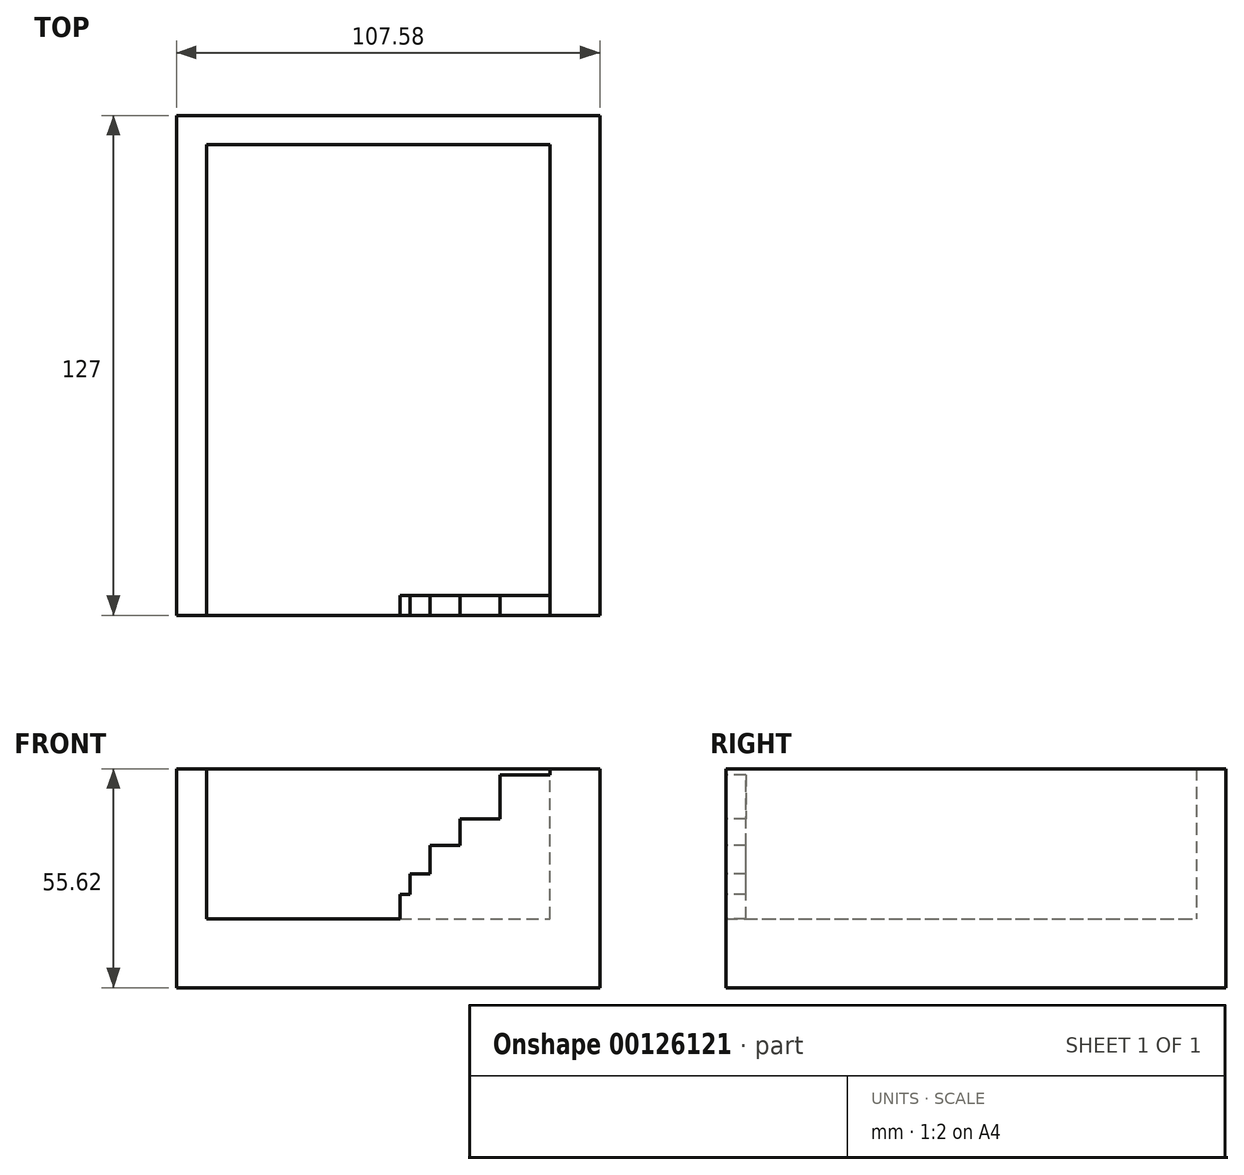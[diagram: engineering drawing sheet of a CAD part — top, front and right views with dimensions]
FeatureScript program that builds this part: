
annotation { "Feature Type Name" : "Feature", "Feature Type Description" : "" }
export const myFeature = defineFeature(function(context is Context, id is Id, definition is map)
    precondition{}
    {
        {
            var Q0;
            Q0=qCreatedBy(makeId("Front.planeOp"),FACE);
            var sketch = newSketch(context, id + "F0", { "sketchPlane" : qUnion([Q0])});
            skLineSegment(sketch, "E0.bottom", {"start": v(-64.64, -20.85) * mm, "end": v(42.94, -20.85) * mm});
            skLineSegment(sketch, "E0.top", {"start": v(-64.64, -3.33) * mm, "end": v(42.94, -3.33) * mm});
            skLineSegment(sketch, "E0.left", {"start": v(-64.64, -20.85) * mm, "end": v(-64.64, -3.33) * mm});
            skLineSegment(sketch, "E0.right", {"start": v(42.94, -20.85) * mm, "end": v(42.94, -3.33) * mm});
            skLineSegment(sketch, "E1.bottom", {"start": v(-64.64, -3.33) * mm, "end": v(-57.02, -3.33) * mm});
            skLineSegment(sketch, "E1.top", {"start": v(-64.64, 34.77) * mm, "end": v(-57.02, 34.77) * mm});
            skLineSegment(sketch, "E1.left", {"start": v(-64.64, -3.33) * mm, "end": v(-64.64, 34.77) * mm});
            skLineSegment(sketch, "E1.right", {"start": v(-57.02, -3.33) * mm, "end": v(-57.02, 34.77) * mm});
            skLineSegment(sketch, "E2.bottom", {"start": v(42.94, -3.33) * mm, "end": v(30.24, -3.33) * mm});
            skLineSegment(sketch, "E2.top", {"start": v(42.94, 34.77) * mm, "end": v(30.24, 34.77) * mm});
            skLineSegment(sketch, "E2.left", {"start": v(42.94, -3.33) * mm, "end": v(42.94, 34.77) * mm});
            skLineSegment(sketch, "E2.right", {"start": v(30.24, -3.33) * mm, "end": v(30.24, 34.77) * mm});
            skSolve(sketch);
        }
        {
            var Q0;
            Q0 = qSketchRegion(id + "F0", true);
            extrude(context, id + "F1", {"entities" : qUnion([Q0]), "depth" : 127 * mm});
        }
        {
            var Q0;
            Q0=makeQuery(id+"F1.opExtrude","SWEPT_FACE",FACE,{"disambiguationData":[OSD([sQuery(id+"F0.wireOp",EDGE,"E0.top")])]});
            var sketch = newSketch(context, id + "F2", { "sketchPlane" : qUnion([Q0])});
            skLineSegment(sketch, "E3.bottom", {"start": v(30.24, 0) * mm, "end": v(-57.02, 0) * mm});
            skLineSegment(sketch, "E3.top", {"start": v(30.24, -7.48) * mm, "end": v(-57.02, -7.48) * mm});
            skLineSegment(sketch, "E3.left", {"start": v(30.24, 0) * mm, "end": v(30.24, -7.48) * mm});
            skLineSegment(sketch, "E3.right", {"start": v(-57.02, 0) * mm, "end": v(-57.02, -7.48) * mm});
            skSolve(sketch);
        }
        {
            var Q0;
            Q0 = qSketchRegion(id + "F2", true);
            extrude(context, id + "F3", {"entities" : qUnion([Q0]), "operationType" : NewBodyOperationType.ADD, "depth" : 38.1 * mm});
        }
        {
            var Q0;
            Q0=makeQuery(id+"F1.opExtrude","CAP_FACE",FACE,{"disambiguationData":[OSD([sQuery(id+"F0.wireOp",EDGE,"E0.bottom"),sQuery(id+"F0.wireOp",EDGE,"E0.top"),sQuery(id+"F0.wireOp",EDGE,"E0.left"),sQuery(id+"F0.wireOp",EDGE,"E0.right"),sQuery(id+"F0.wireOp",EDGE,"E1.top"),sQuery(id+"F0.wireOp",EDGE,"E1.left"),sQuery(id+"F0.wireOp",EDGE,"E1.right"),sQuery(id+"F0.wireOp",EDGE,"E2.top"),sQuery(id+"F0.wireOp",EDGE,"E2.left"),sQuery(id+"F0.wireOp",EDGE,"E2.right")])],"isStart":false});
            var sketch = newSketch(context, id + "F4", { "sketchPlane" : qUnion([Q0])});
            skSolve(sketch);
        }
        {
            var Q0;
            Q0=makeQuery(id+"F4.imprint","IMPRINT",FACE,{"disambiguationData":[TD([[makeQuery(id+"F4.imprint","IMPRINT",EDGE,{"derivedFrom":makeQuery(id+"F1.opExtrude","CAP_EDGE",EDGE,{"disambiguationData":[OSD([sQuery(id+"F0.wireOp",EDGE,"E0.bottom")])],"isStart":false})}),1.0]])]});
            var sketch = newSketch(context, id + "F5", { "sketchPlane" : qUnion([Q0])});
            skLineSegment(sketch, "E4.bottom", {"start": v(30.24, 33.25) * mm, "end": v(17.54, 33.25) * mm});
            skLineSegment(sketch, "E4.top", {"start": v(30.24, -3.33) * mm, "end": v(17.54, -3.33) * mm});
            skLineSegment(sketch, "E4.left", {"start": v(30.24, 33.25) * mm, "end": v(30.24, -3.33) * mm});
            skLineSegment(sketch, "E4.right", {"start": v(17.54, 33.25) * mm, "end": v(17.54, -3.33) * mm});
            skLineSegment(sketch, "E5.bottom", {"start": v(17.54, -3.33) * mm, "end": v(7.38, -3.33) * mm});
            skLineSegment(sketch, "E5.top", {"start": v(17.54, 22.02) * mm, "end": v(7.38, 22.02) * mm});
            skLineSegment(sketch, "E5.left", {"start": v(17.54, -3.33) * mm, "end": v(17.54, 22.02) * mm});
            skLineSegment(sketch, "E5.right", {"start": v(7.38, -3.33) * mm, "end": v(7.38, 22.02) * mm});
            skLineSegment(sketch, "E6.bottom", {"start": v(7.38, -3.33) * mm, "end": v(-0.24, -3.33) * mm});
            skLineSegment(sketch, "E6.top", {"start": v(7.38, 15.33) * mm, "end": v(-0.24, 15.33) * mm});
            skLineSegment(sketch, "E6.left", {"start": v(7.38, -3.33) * mm, "end": v(7.38, 15.33) * mm});
            skLineSegment(sketch, "E6.right", {"start": v(-0.24, -3.33) * mm, "end": v(-0.24, 15.33) * mm});
            skLineSegment(sketch, "E7.bottom", {"start": v(-0.24, -3.33) * mm, "end": v(-5.32, -3.33) * mm});
            skLineSegment(sketch, "E7.top", {"start": v(-0.24, 8.12) * mm, "end": v(-5.32, 8.12) * mm});
            skLineSegment(sketch, "E7.left", {"start": v(-0.24, -3.33) * mm, "end": v(-0.24, 8.12) * mm});
            skLineSegment(sketch, "E7.right", {"start": v(-5.32, -3.33) * mm, "end": v(-5.32, 8.12) * mm});
            skLineSegment(sketch, "E8.bottom", {"start": v(-5.32, -3.33) * mm, "end": v(-7.86, -3.33) * mm});
            skLineSegment(sketch, "E8.top", {"start": v(-5.32, 2.82) * mm, "end": v(-7.86, 2.82) * mm});
            skLineSegment(sketch, "E8.left", {"start": v(-5.32, -3.33) * mm, "end": v(-5.32, 2.82) * mm});
            skLineSegment(sketch, "E8.right", {"start": v(-7.86, -3.33) * mm, "end": v(-7.86, 2.82) * mm});
            skSolve(sketch);
        }
        {
            var Q0;
            Q0=makeQuery(id+"F5.imprint","IMPRINT",FACE,{"disambiguationData":[TD([[makeQuery(id+"F5.imprint","IMPRINT",EDGE,{"derivedFrom":sQuery(id+"F5.wireOp",EDGE,"E4.bottom")}),1.0]])]});
            var Q1;
            Q1=makeQuery(id+"F5.imprint","IMPRINT",FACE,{"disambiguationData":[TD([[makeQuery(id+"F5.imprint","IMPRINT",EDGE,{"derivedFrom":sQuery(id+"F5.wireOp",EDGE,"E5.bottom")}),1.0]])]});
            var Q2;
            Q2=makeQuery(id+"F5.imprint","IMPRINT",FACE,{"disambiguationData":[TD([[makeQuery(id+"F5.imprint","IMPRINT",EDGE,{"derivedFrom":sQuery(id+"F5.wireOp",EDGE,"E6.bottom")}),1.0]])]});
            var Q3;
            Q3=makeQuery(id+"F5.imprint","IMPRINT",FACE,{"disambiguationData":[TD([[makeQuery(id+"F5.imprint","IMPRINT",EDGE,{"derivedFrom":sQuery(id+"F5.wireOp",EDGE,"E7.bottom")}),1.0]])]});
            var Q4;
            Q4=makeQuery(id+"F5.imprint","IMPRINT",FACE,{"disambiguationData":[TD([[makeQuery(id+"F5.imprint","IMPRINT",EDGE,{"derivedFrom":sQuery(id+"F5.wireOp",EDGE,"E8.bottom")}),1.0]])]});
            extrude(context, id + "F6", {"entities" : qUnion([Q0, Q1, Q2, Q3, Q4]), "operationType" : NewBodyOperationType.ADD, "oppositeDirection" : true, "depth" : 5.08 * mm});
        }
    });
